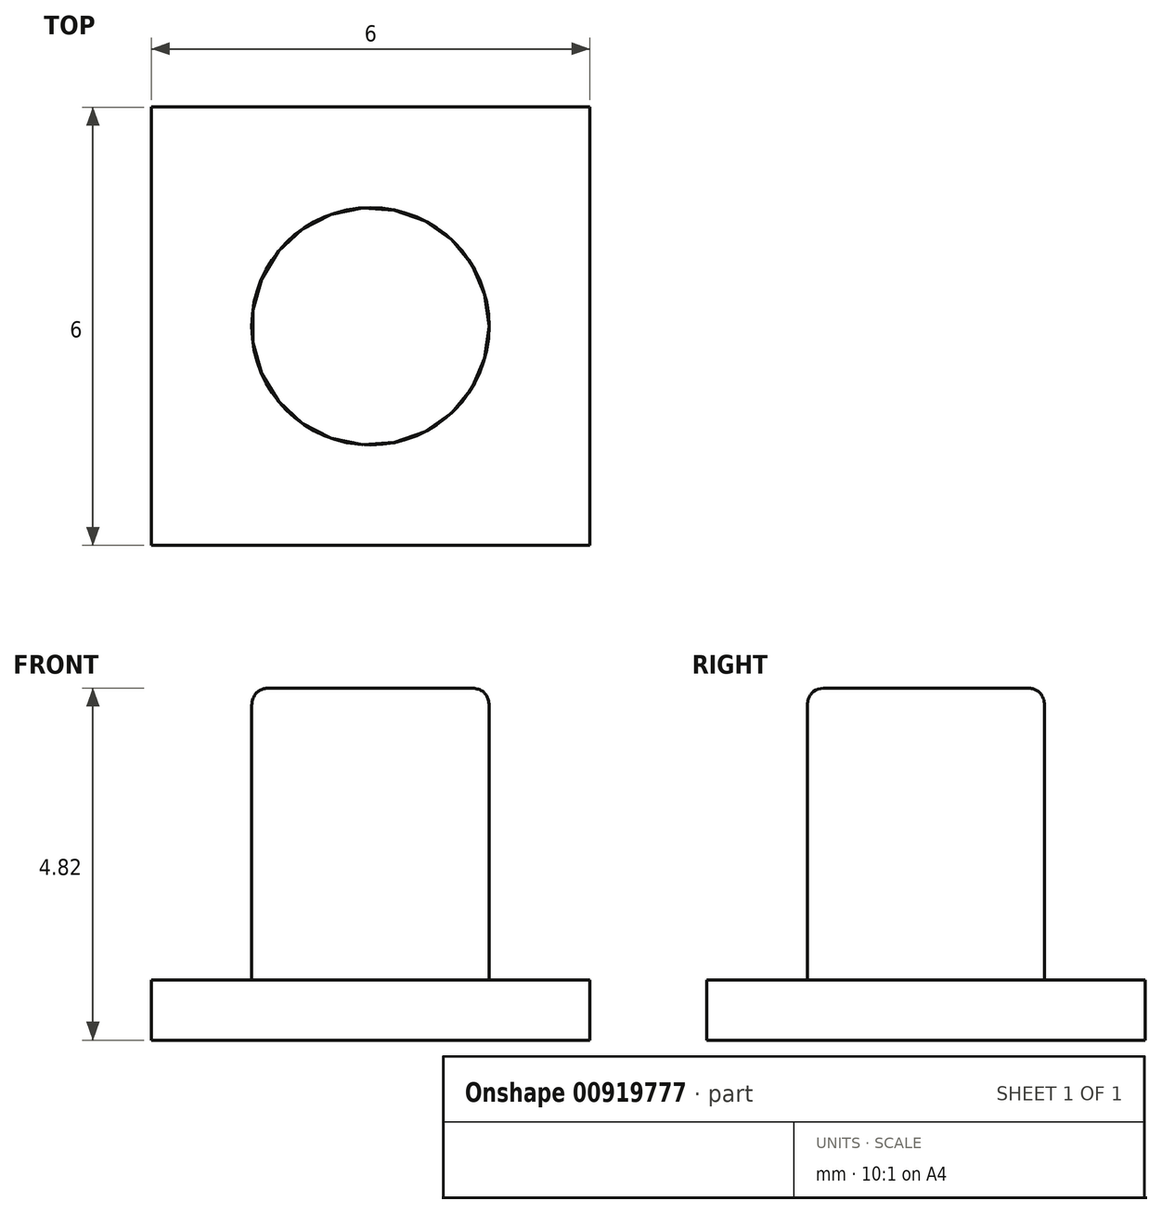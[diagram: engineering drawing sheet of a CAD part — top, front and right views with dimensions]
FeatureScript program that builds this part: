
annotation { "Feature Type Name" : "Feature", "Feature Type Description" : "" }
export const myFeature = defineFeature(function(context is Context, id is Id, definition is map)
    precondition{}
    {
        {
            var Q0;
            Q0=qCreatedBy(makeId("Top.planeOp"),FACE);
            var sketch = newSketch(context, id + "F0", { "sketchPlane" : qUnion([Q0])});
            skLineSegment(sketch, "E0.bottom", {"start": v(-3.61, -7.1) * mm, "end": v(2.39, -7.1) * mm});
            skLineSegment(sketch, "E0.top", {"start": v(-3.61, -13.1) * mm, "end": v(2.39, -13.1) * mm});
            skLineSegment(sketch, "E0.left", {"start": v(-3.61, -7.1) * mm, "end": v(-3.61, -13.1) * mm});
            skLineSegment(sketch, "E0.right", {"start": v(2.39, -7.1) * mm, "end": v(2.39, -13.1) * mm});
            skSolve(sketch);
        }
        {
            var Q0;
            Q0 = qSketchRegion(id + "F0", true);
            extrude(context, id + "F1", {"entities" : qUnion([Q0]), "depth" : .82 * mm, "offsetDistance" : 25 * mm});
        }
        {
            var Q0;
            Q0=makeQuery(id+"F1.opExtrude","CAP_FACE",FACE,{"disambiguationData":[OSD([sQuery(id+"F0.wireOp",EDGE,"E0.bottom"),sQuery(id+"F0.wireOp",EDGE,"E0.top"),sQuery(id+"F0.wireOp",EDGE,"E0.left"),sQuery(id+"F0.wireOp",EDGE,"E0.right")])],"isStart":false});
            var sketch = newSketch(context, id + "F2", { "sketchPlane" : qUnion([Q0])});
            skCircle(sketch, "E1", {"center": v(-0.61, -10.1) * mm, "radius": 1.63 * mm});
            skPoint(sketch, "E1.centerSnap0", {"position": v(-0.61, -7.1) * mm});
            skPoint(sketch, "E1.centerSnap1", {"position": v(2.39, -10.1) * mm});
            skSolve(sketch);
        }
        {
            var Q0;
            Q0=makeQuery(id+"F2.imprint","IMPRINT",FACE,{"disambiguationData":[TD([[makeQuery(id+"F2.imprint","IMPRINT",EDGE,{"derivedFrom":sQuery(id+"F2.wireOp",EDGE,"E1")}),1.0]])]});
            extrude(context, id + "F3", {"entities" : qUnion([Q0]), "operationType" : NewBodyOperationType.ADD, "depth" : 4 * mm, "offsetDistance" : 25 * mm});
        }
        {
            var Q0;
            Q0=makeQuery(id+"F1.opExtrude","CAP_FACE",FACE,{"disambiguationData":[OSD([sQuery(id+"F0.wireOp",EDGE,"E0.bottom"),sQuery(id+"F0.wireOp",EDGE,"E0.top"),sQuery(id+"F0.wireOp",EDGE,"E0.left"),sQuery(id+"F0.wireOp",EDGE,"E0.right")])],"isStart":false});
            var sketch = newSketch(context, id + "F4", { "sketchPlane" : qUnion([Q0])});
            skPoint(sketch, "E2.startSnap0", {"position": v(-3.61, -10.1) * mm});
            skPoint(sketch, "E2.startSnap1", {"position": v(-0.61, -13.1) * mm});
            skArc(sketch, "E3", {"start": v(-0.61, -8.35) * mm, "mid": v(-2.36, -10.1) * mm, "end": v(-0.61, -11.85) * mm});
            skLineSegment(sketch, "E4", {"start": v(-0.61, -11.85) * mm, "end": v(-0.61, -8.35) * mm});
            skSolve(sketch);
        }
        {
            var Q0;
            Q0=makeQuery(id+"F3.opExtrude","CAP_EDGE",EDGE,{"disambiguationData":[OSD([sQuery(id+"F2.wireOp",EDGE,"E1")])],"isStart":false});
            fillet(context, id + "F5", {"entities" : qUnion([Q0]), "radius" : 0.27 * mm, "rho" : .5, "crossSection" : FilletCrossSection.CONIC, "allowEdgeOverflow" : false});
        }
    });
